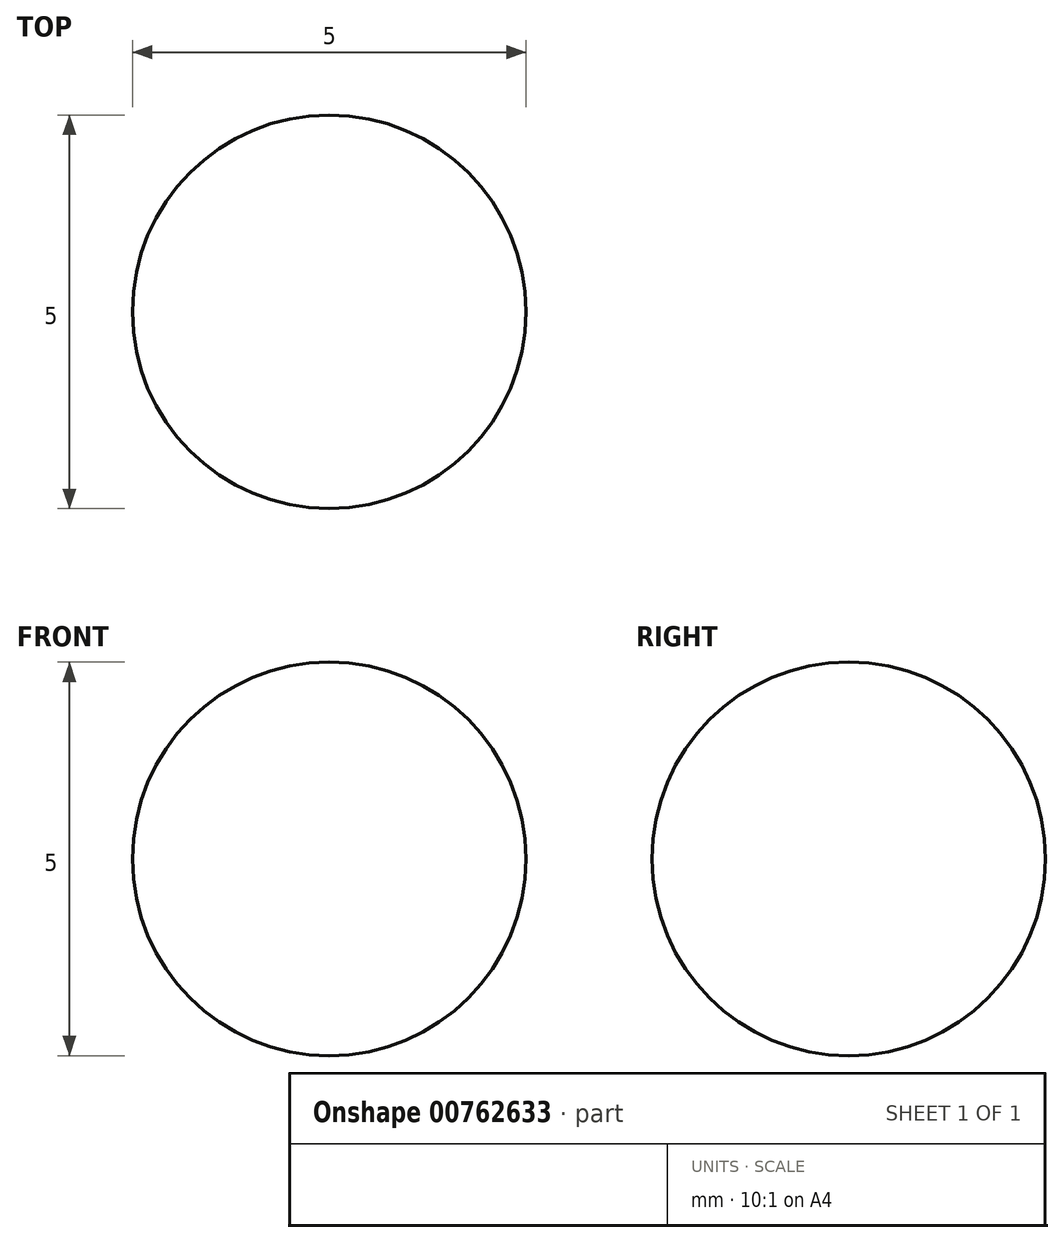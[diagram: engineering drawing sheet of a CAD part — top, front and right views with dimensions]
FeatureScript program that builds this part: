
annotation { "Feature Type Name" : "Feature", "Feature Type Description" : "" }
export const myFeature = defineFeature(function(context is Context, id is Id, definition is map)
    precondition{}
    {
        {
            var Q0;
            Q0=qCreatedBy(makeId("Front.planeOp"),FACE);
            var sketch = newSketch(context, id + "F0", { "sketchPlane" : qUnion([Q0])});
            skArc(sketch, "E0", {"start": v(0, -2.5) * mm, "mid": v(2.5, 0) * mm, "end": v(0, 2.5) * mm});
            skLineSegment(sketch, "E1", {"start": v(0, 2.5) * mm, "end": v(0, -2.5) * mm});
            skSolve(sketch);
        }
        {
            var Q0;
            Q0=qSketchRegion(id+"F0",true);
            var Q1;
            Q1=sQuery(id+"F0.wireOp",EDGE,"E1");
            revolve(context, id + "F1", {"surfaceOperationType" : NewSurfaceOperationType.NEW, "entities" : qUnion([Q0]), "axis" : qUnion([Q1]), "revolveType" : RevolveType.FULL});
        }
    });
